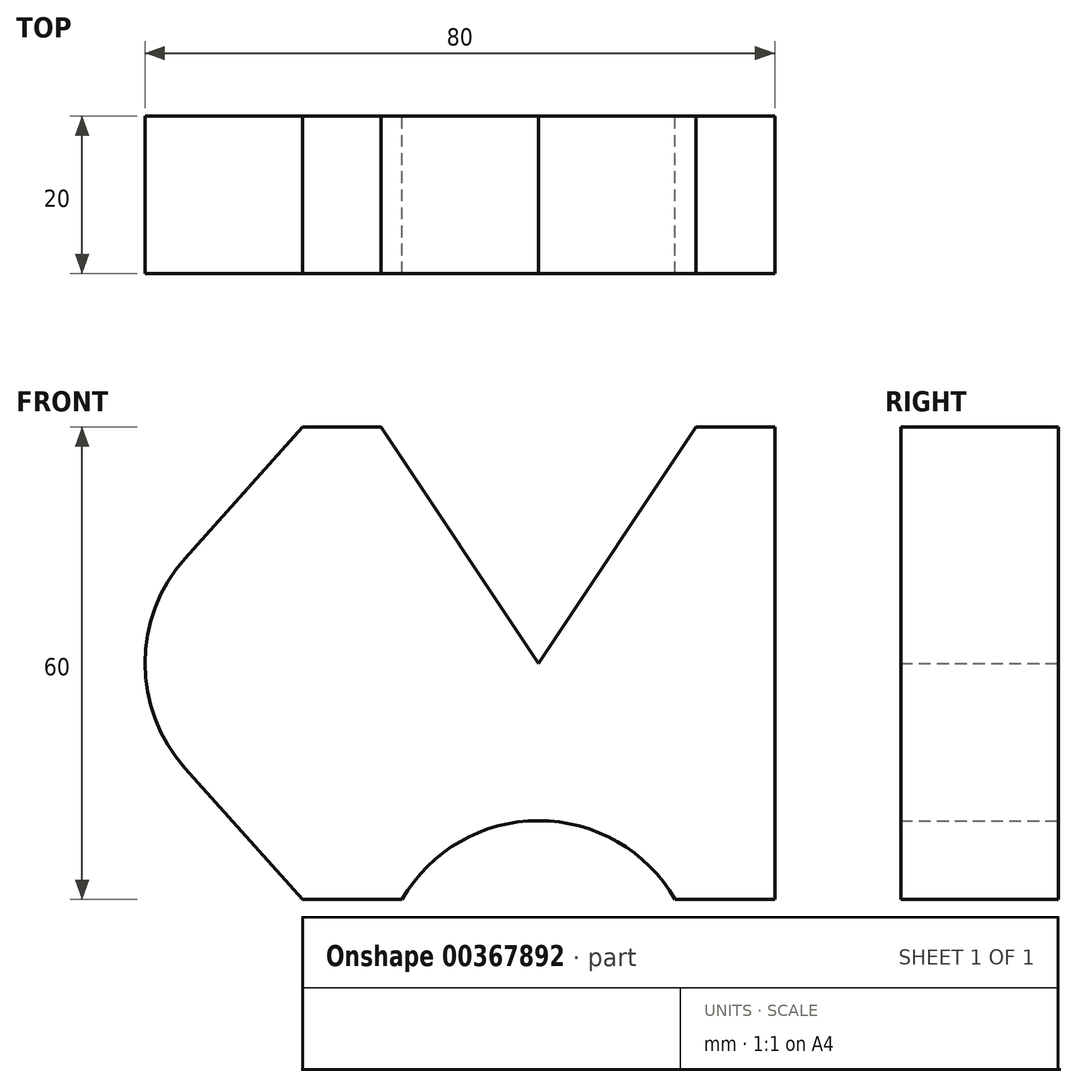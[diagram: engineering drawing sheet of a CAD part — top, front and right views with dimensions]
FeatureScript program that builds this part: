
annotation { "Feature Type Name" : "Feature", "Feature Type Description" : "" }
export const myFeature = defineFeature(function(context is Context, id is Id, definition is map)
    precondition{}
    {
        {
            var Q0;
            Q0=qCreatedBy(makeId("Front.planeOp"),FACE);
            var sketch = newSketch(context, id + "F0", { "sketchPlane" : qUnion([Q0])});
            skLineSegment(sketch, "E0", {"start": v(0, 0) * mm, "end": v(20, 30) * mm});
            skLineSegment(sketch, "E1", {"start": v(20, 30) * mm, "end": v(30, 30) * mm});
            skLineSegment(sketch, "E2", {"start": v(30, 30) * mm, "end": v(30, -30) * mm});
            skLineSegment(sketch, "E3", {"start": v(30, -30) * mm, "end": v(17.32, -30) * mm});
            skArc(sketch, "E4", {"start": v(17.32, -30) * mm, "mid": v(0, -20) * mm, "end": v(-17.32, -30) * mm});
            skLineSegment(sketch, "E5", {"start": v(-17.32, -30) * mm, "end": v(-30, -30) * mm});
            skLineSegment(sketch, "E6", {"start": v(-30, -30) * mm, "end": v(-44.9, -13.33) * mm});
            skLineSegment(sketch, "E7", {"start": v(0, 0) * mm, "end": v(-20, 30) * mm});
            skLineSegment(sketch, "E8", {"start": v(-20, 30) * mm, "end": v(-30, 30) * mm});
            skLineSegment(sketch, "E9", {"start": v(-30, 30) * mm, "end": v(-44.9, 13.33) * mm});
            skArc(sketch, "E10", {"start": v(-44.9, 13.33) * mm, "mid": v(-50, 0) * mm, "end": v(-44.9, -13.33) * mm});
            skLineSegment(sketch, "E11", {"start": v(-30, 30) * mm, "end": v(-30, -30) * mm, "construction": true});
            skSolve(sketch);
        }
        {
            var Q0;
            Q0 = qSketchRegion(id + "F0", true);
            extrude(context, id + "F1", {"entities" : qUnion([Q0]), "depth" : 20 * mm});
        }
    });
